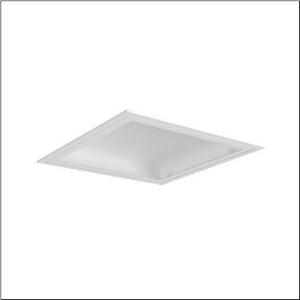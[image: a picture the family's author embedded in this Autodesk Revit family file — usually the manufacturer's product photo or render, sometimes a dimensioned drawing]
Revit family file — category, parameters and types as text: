
# Revit family: mira_21_51fr427a432a
name_source: partatom
category: Lighting Fixtures
units: mm (PartAtom-declared; Revit-internal decimal feet)

## family parameters
Cut with Voids When Loaded = No
Host = Face
Light Source = No
Part Type = Normal
Room Calculation Point = No
Round Connector Dimension = Use Diameter
Shared = No

## types (1)
- Mira 21 (1 x LED, 3220 lm, 23 W, 4000K)
    Apparent Load = 23 VA
    CIE Flux Codes = 50 81 97 100 100
    Color Rendering = 80
    Color Temperature = 4000K
    Default Elevation = 1800 mm
    Description = Mira 21, clean room luminaire, primary light control with reflector, primary optical cover: cover, of PC, light emission: direct distribution, primary light characteristic: symmetric, installation type: recessed, LED, rated luminous flux: 3.220lm, luminous efficacy: 140lm/W, light colour: 840, colour temperature: 4000K, control gear: ON/OFF, with terminal, 3-pole, max. 2.5mm², mains connection: 230V, AC, 50/60Hz, rated input power: 23W, luminaire housing, of sheet steel, coated, pure white (RAL 9010), with concealed spring brackets, module: M625, length: 623mm, width: 623mm, height: 115mm, protection rating (complete): IP54, insulation class (complete): insulation class I (protective earthing), certification: CE, UKCA, permissible operating ambient temperature: -5..+40°C, standard: EN 50419, packaging unit: 1 piece
    Height = 0 mm  [stored 0 ft]
    Lamp = 1 x LED
    Lamp Light Flux = 3220 lm
    Lamp Power = 23 W
    Lamp count = 1
    Length = 625 mm
    Luminous efficacy = 140 lm/W
    Manufacturer = Siteco
    ModVariant = No
    Model = 51FR427A432A
    Mounting Place = Ceiling
    Mounting Type = Recessed
    Number of Poles = 1
    OnlyDefault = Yes
    Power Factor = 1
    Product Name = Mira 21
    Product group = clean room luminaire | ceiling recessed
    ProductGroupID = 402
    Protection Class = Protection class I
    Protection Degree = IP 54
    RLX_Detail_Level = 1
    RLX_Emergency_Light_Flux = 0 lm
    RLX_Emergency_Type = 0
    RLX_Emergency_Type_DB = No
    RlxData = <blob elided: 13381 chars, md5=91706861>
    Socket = socket
    Standby Power = 0 W
    System Light Flux = 3220 lm
    System Power = 23 W
    Type Comments = Product without accessories
    Type Image = l_1007109.jpg
    URL = http://relux.com
    VarID = ---
    Voltage = 0 V
    Weight = 0.00 kg
    Width = 625 mm

note: [stored X ft] marks values corroborated as IEEE doubles in the binary element streams (Revit-internal decimal feet)

## geometry (parser evidence)
native form markers: Sweep x8
no freeform markers — native parametric forms only
